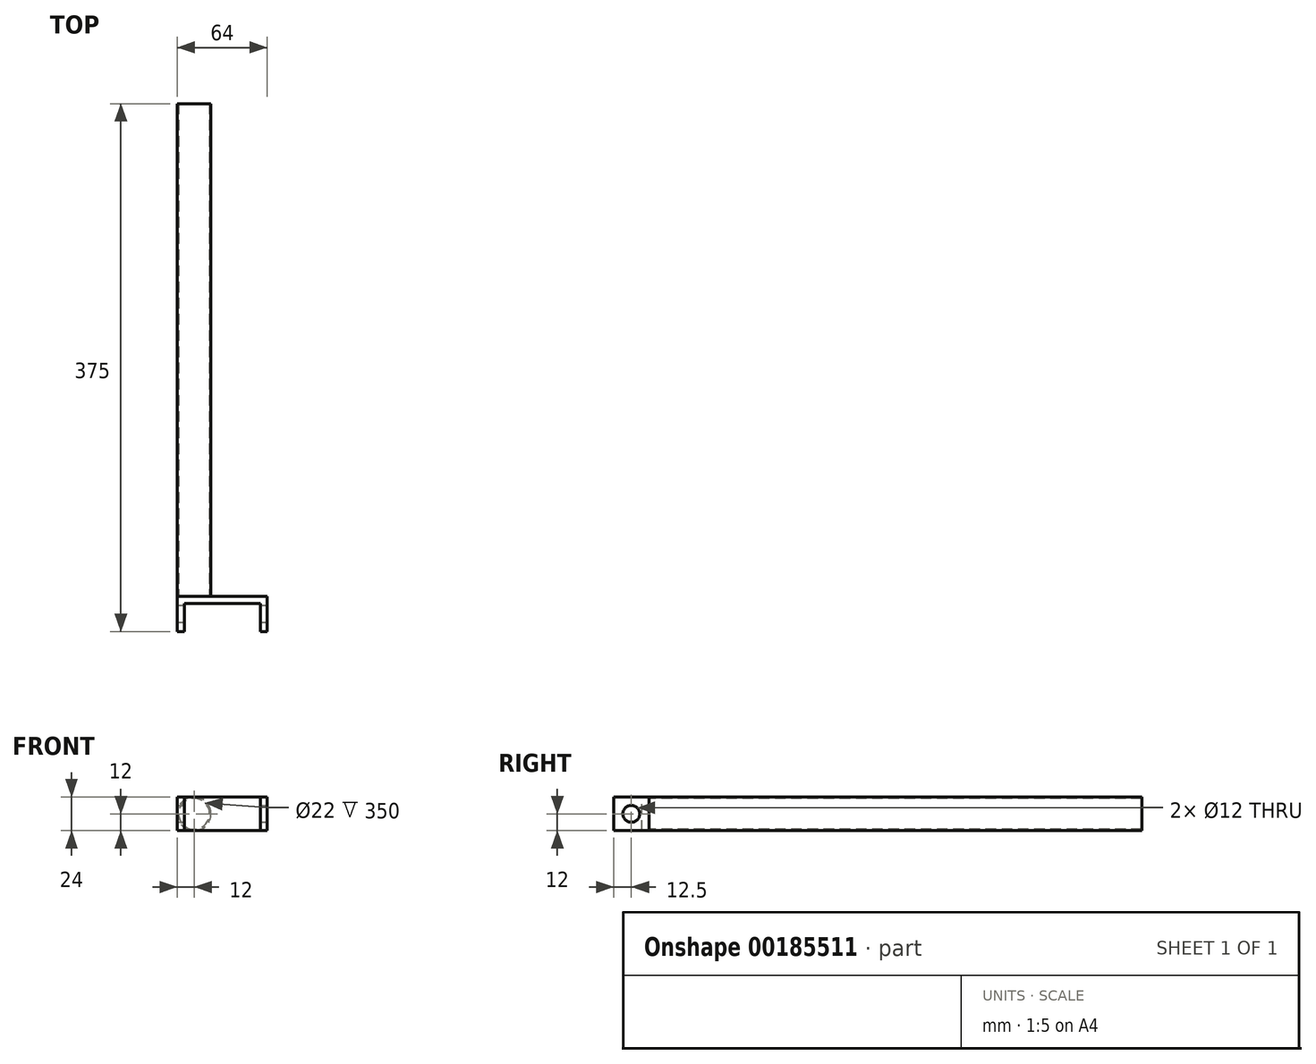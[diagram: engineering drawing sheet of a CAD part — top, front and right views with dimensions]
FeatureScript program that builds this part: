
annotation { "Feature Type Name" : "Feature", "Feature Type Description" : "" }
export const myFeature = defineFeature(function(context is Context, id is Id, definition is map)
    precondition{}
    {
        {
            var Q0;
            Q0=qCreatedBy(makeId("Front.planeOp"),FACE);
            var sketch = newSketch(context, id + "F0", { "sketchPlane" : qUnion([Q0])});
            skCircle(sketch, "E0", {"center": v(-20, 0) * mm, "radius": 12 * mm});
            skCircle(sketch, "E1.MirrorC", {"center": v(20, 0) * mm, "radius": 12 * mm});
            skCircle(sketch, "E2.0", {"center": v(-20, 0) * mm, "radius": 11 * mm});
            skCircle(sketch, "E3.MirrorC", {"center": v(20, 0) * mm, "radius": 11 * mm});
            skSolve(sketch);
        }
        {
            var Q0;
            Q0=makeQuery(id+"F0.imprint","IMPRINT",FACE,{"disambiguationData":[TD([[makeQuery(id+"F0.imprint","IMPRINT",EDGE,{"derivedFrom":sQuery(id+"F0.wireOp",EDGE,"E0")}),1.0]])]});
            var Q1;
            Q1=makeQuery(id+"F0.imprint","IMPRINT",FACE,{"disambiguationData":[TD([[makeQuery(id+"F0.imprint","IMPRINT",EDGE,{"derivedFrom":sQuery(id+"F0.wireOp",EDGE,"E1.MirrorC")}),-1.0]])]});
            extrude(context, id + "F1", {"entities" : qUnion([Q0, Q1]), "oppositeDirection" : true, "depth" : 350 * mm});
        }
        {
            var Q0;
            Q0=qCreatedBy(makeId("Front.planeOp"),FACE);
            var sketch = newSketch(context, id + "F2", { "sketchPlane" : qUnion([Q0])});
            skLineSegment(sketch, "E4.bottom", {"start": v(32, 12) * mm, "end": v(-32, 12) * mm});
            skLineSegment(sketch, "E4.top", {"start": v(32, -12) * mm, "end": v(-32, -12) * mm});
            skLineSegment(sketch, "E4.left", {"start": v(32, 12) * mm, "end": v(32, -12) * mm});
            skLineSegment(sketch, "E4.right", {"start": v(-32, 12) * mm, "end": v(-32, -12) * mm});
            skPoint(sketch, "E4.middle", {"position": v(0, 0) * mm});
            skSolve(sketch);
        }
        {
            var Q0;
            Q0=makeQuery(id+"F2.imprint","IMPRINT",FACE,{"disambiguationData":[TD([[makeQuery(id+"F2.imprint","IMPRINT",EDGE,{"derivedFrom":sQuery(id+"F2.wireOp",EDGE,"E4.bottom")}),1.0]])]});
            extrude(context, id + "F3", {"entities" : qUnion([Q0]), "depth" : 25 * mm});
        }
        {
            var Q0;
            Q0=makeQuery(id+"F3.opExtrude","SWEPT_FACE",FACE,{"disambiguationData":[OSD([sQuery(id+"F2.wireOp",EDGE,"E4.left")])]});
            var sketch = newSketch(context, id + "F4", { "sketchPlane" : qUnion([Q0])});
            skCircle(sketch, "E5", {"center": v(-12.5, 0) * mm, "radius": 6 * mm});
            skSolve(sketch);
        }
        {
            var Q0;
            Q0=makeQuery(id+"F4.imprint","IMPRINT",FACE,{"disambiguationData":[TD([[makeQuery(id+"F4.imprint","IMPRINT",EDGE,{"derivedFrom":sQuery(id+"F4.wireOp",EDGE,"E5")}),1.0]])]});
            extrude(context, id + "F5", {"entities" : qUnion([Q0]), "operationType" : NewBodyOperationType.REMOVE, "endBound" : BoundingType.THROUGH_ALL, "oppositeDirection" : true, "depth" : 25 * mm});
        }
        {
            var Q0;
            Q0=makeQuery(id+"F3.opExtrude","SWEPT_FACE",FACE,{"disambiguationData":[OSD([sQuery(id+"F2.wireOp",EDGE,"E4.bottom")])]});
            var sketch = newSketch(context, id + "F6", { "sketchPlane" : qUnion([Q0])});
            skLineSegment(sketch, "E6.top", {"start": v(27, -5) * mm, "end": v(-27, -5) * mm});
            skLineSegment(sketch, "E6.left", {"start": v(27, -28) * mm, "end": v(27, -5) * mm});
            skLineSegment(sketch, "E6.right", {"start": v(-27, -28) * mm, "end": v(-27, -5) * mm});
            skPoint(sketch, "E6.middle", {"position": v(0, -13.78) * mm});
            skLineSegment(sketch, "E7", {"start": v(-27, -28) * mm, "end": v(27, -28) * mm});
            skSolve(sketch);
        }
        {
            var Q0;
            {var subQ0=sQuery(id+"F6.wireOp",EDGE,"E7");Q0=makeQuery(id+"F6.imprint","IMPRINT",FACE,{"disambiguationData":[TD([[makeQuery(id+"F6.imprint","IMPRINT",EDGE,{"derivedFrom":subQ0}),1.0]])]});}
            var Q1;
            {var subQ0=sQuery(id+"F6.wireOp",EDGE,"E6.top");Q1=makeQuery(id+"F6.imprint","IMPRINT",FACE,{"disambiguationData":[TD([[makeQuery(id+"F6.imprint","IMPRINT",EDGE,{"derivedFrom":subQ0}),1.0]])]});}
            extrude(context, id + "F7", {"entities" : qUnion([Q0, Q1]), "operationType" : NewBodyOperationType.REMOVE, "endBound" : BoundingType.THROUGH_ALL, "oppositeDirection" : true, "depth" : 25 * mm});
        }
    });
